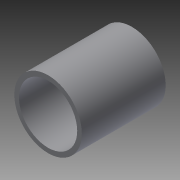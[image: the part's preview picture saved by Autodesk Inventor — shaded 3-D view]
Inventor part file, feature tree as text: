
AUTODESK INVENTOR PART (.ipt)
format: ipt  version: 2013 (Build 170138000, 138)  size: 84,480 bytes
history: native  units: in
note: dims shown in document units (in); Inventor stores cm internally (conversion verified against a paired STEP export)
features: extrude x1, sketch x1
ambient origin geometry x8: Origin, YZ Plane, XZ Plane, XY Plane, X Axis, Y Axis, Z Axis, Center Point
bodies: Solid1 (feature_tree)
feature tree (2):
  extrude  "Extrusion1"  Depth=1.25in
  sketch  "Sketch1"  dims[d0=1.45in d1=1.25in d2=1.8in d3=0.0in]
